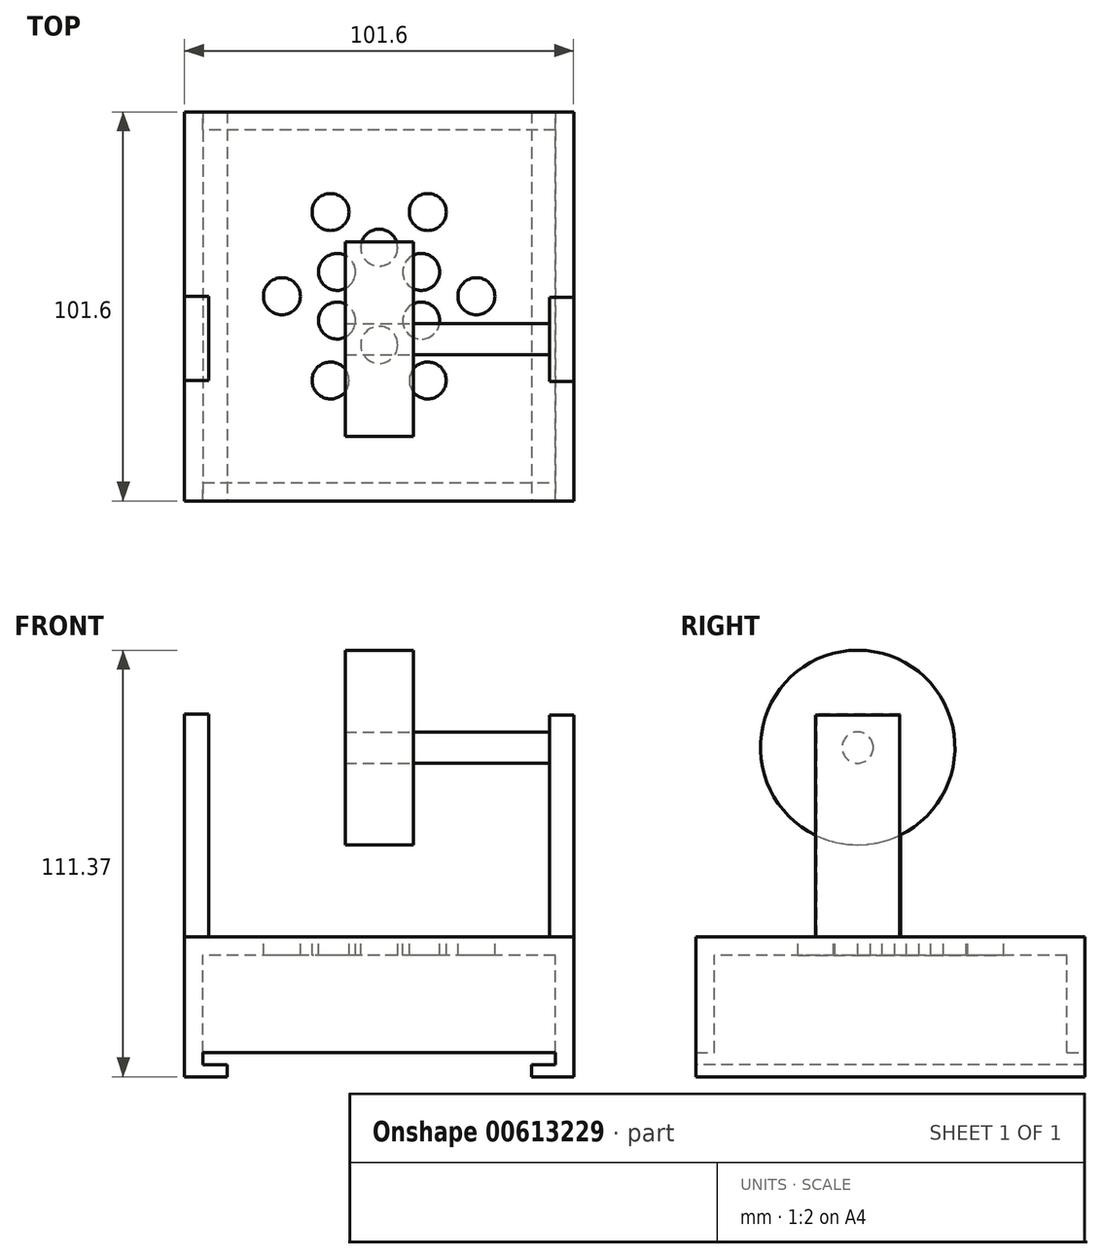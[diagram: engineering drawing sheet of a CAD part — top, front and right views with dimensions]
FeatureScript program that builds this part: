
annotation { "Feature Type Name" : "Feature", "Feature Type Description" : "" }
export const myFeature = defineFeature(function(context is Context, id is Id, definition is map)
    precondition{}
    {
        {
            var Q0;
            Q0=qCreatedBy(makeId("Top.planeOp"),FACE);
            var sketch = newSketch(context, id + "F0", { "sketchPlane" : qUnion([Q0])});
            skLineSegment(sketch, "E0", {"start": v(-108.53, 59.8) * mm, "end": v(-108.53, -41.8) * mm});
            skLineSegment(sketch, "E1", {"start": v(-108.53, -41.8) * mm, "end": v(-6.93, -41.8) * mm});
            skLineSegment(sketch, "E2", {"start": v(-6.93, -41.8) * mm, "end": v(-6.93, 59.8) * mm});
            skLineSegment(sketch, "E3", {"start": v(-6.93, 59.8) * mm, "end": v(-108.53, 59.8) * mm});
            skSolve(sketch);
        }
        {
            var Q0;
            Q0=makeQuery(id+"F0.imprint","IMPRINT",FACE,{"disambiguationData":[TD([[makeQuery(id+"F0.imprint","IMPRINT",EDGE,{"derivedFrom":sQuery(id+"F0.wireOp",EDGE,"E0")}),1.0]])]});
            extrude(context, id + "F1", {"entities" : qUnion([Q0]), "oppositeDirection" : true, "depth" : 30.16 * mm, "offsetDistance" : 25.4 * mm});
        }
        {
            var Q0;
            Q0=makeQuery(id+"F1.opExtrude","SWEPT_FACE",FACE,{"disambiguationData":[OSD([sQuery(id+"F0.wireOp",EDGE,"E2")])]});
            var sketch = newSketch(context, id + "F2", { "sketchPlane" : qUnion([Q0])});
            skLineSegment(sketch, "E4", {"start": v(-10.59, 0) * mm, "end": v(-10.59, 57.92) * mm});
            skLineSegment(sketch, "E5", {"start": v(-10.59, 57.92) * mm, "end": v(11.37, 57.92) * mm});
            skLineSegment(sketch, "E6", {"start": v(11.37, 57.92) * mm, "end": v(11.37, 0) * mm});
            skLineSegment(sketch, "E7", {"start": v(11.37, 0) * mm, "end": v(-10.59, 0) * mm});
            skSolve(sketch);
        }
        {
            var Q0;
            Q0 = qSketchRegion(id + "F2", true);
            extrude(context, id + "F3", {"entities" : qUnion([Q0]), "oppositeDirection" : true, "depth" : 6.35 * mm, "offsetDistance" : 25.4 * mm});
        }
        {
            var Q0;
            Q0=makeQuery(id+"F1.opExtrude","SWEPT_FACE",FACE,{"disambiguationData":[OSD([sQuery(id+"F0.wireOp",EDGE,"E0")])]});
            var sketch = newSketch(context, id + "F4", { "sketchPlane" : qUnion([Q0])});
            skLineSegment(sketch, "E8", {"start": v(-11.64, 0) * mm, "end": v(-11.64, 58.18) * mm});
            skLineSegment(sketch, "E9", {"start": v(-11.64, 58.18) * mm, "end": v(10.33, 58.18) * mm});
            skLineSegment(sketch, "E10", {"start": v(10.33, 58.18) * mm, "end": v(10.33, 0) * mm});
            skLineSegment(sketch, "E11", {"start": v(10.33, 0) * mm, "end": v(-11.64, 0) * mm});
            skSolve(sketch);
        }
        {
            var Q0;
            Q0=makeQuery(id+"F4.imprint","IMPRINT",FACE,{"disambiguationData":[TD([[makeQuery(id+"F4.imprint","IMPRINT",EDGE,{"derivedFrom":sQuery(id+"F4.wireOp",EDGE,"E8")}),-1.0]])]});
            extrude(context, id + "F5", {"entities" : qUnion([Q0]), "oppositeDirection" : true, "depth" : 6.35 * mm, "offsetDistance" : 25.4 * mm});
        }
        {
            var Q0;
            Q0=makeQuery(id+"F1.opExtrude","CAP_FACE",FACE,{"disambiguationData":[OSD([sQuery(id+"F0.wireOp",EDGE,"E0"),sQuery(id+"F0.wireOp",EDGE,"E1"),sQuery(id+"F0.wireOp",EDGE,"E2"),sQuery(id+"F0.wireOp",EDGE,"E3")])],"isStart":true});
            var sketch = newSketch(context, id + "F6", { "sketchPlane" : qUnion([Q0])});
            skPoint(sketch, "E12.cCircle.centerSnap0", {"position": v(-57.73, -41.8) * mm});
            skLineSegment(sketch, "E12.4", {"start": v(-70.43, 33.63) * mm, "end": v(-45.03, 33.63) * mm});
            skPoint(sketch, "E13.cCircle.perimeterSnap0", {"position": v(-57.73, -10.36) * mm});
            skPoint(sketch, "E13.0.startSnap0", {"position": v(-57.73, -10.36) * mm});
            skCircle(sketch, "E14", {"center": v(-70.43, -10.36) * mm, "radius": 4.83 * mm});
            skCircle(sketch, "E15.1.0", {"center": v(-45.03, -10.36) * mm, "radius": 4.83 * mm});
            skCircle(sketch, "E15.2.0", {"center": v(-32.33, 11.64) * mm, "radius": 4.83 * mm});
            skCircle(sketch, "E15.3.0", {"center": v(-45.03, 33.63) * mm, "radius": 4.83 * mm});
            skCircle(sketch, "E15.4.0", {"center": v(-70.43, 33.63) * mm, "radius": 4.83 * mm});
            skCircle(sketch, "E15.5.0", {"center": v(-83.13, 11.64) * mm, "radius": 4.83 * mm});
            skPoint(sketch, "E15.center", {"position": v(-57.73, 11.64) * mm});
            skCircle(sketch, "E16", {"center": v(-57.73, -1.06) * mm, "radius": 4.83 * mm});
            skCircle(sketch, "E17.1.0", {"center": v(-46.73, 5.29) * mm, "radius": 4.83 * mm});
            skCircle(sketch, "E17.2.0", {"center": v(-46.73, 17.99) * mm, "radius": 4.83 * mm});
            skCircle(sketch, "E17.3.0", {"center": v(-57.73, 24.34) * mm, "radius": 4.83 * mm});
            skCircle(sketch, "E17.4.0", {"center": v(-68.73, 17.99) * mm, "radius": 4.83 * mm});
            skCircle(sketch, "E17.5.0", {"center": v(-68.73, 5.29) * mm, "radius": 4.83 * mm});
            skSolve(sketch);
        }
        {
            var Q0;
            Q0=makeQuery(id+"F1.opExtrude","CAP_FACE",FACE,{"disambiguationData":[OSD([sQuery(id+"F0.wireOp",EDGE,"E0"),sQuery(id+"F0.wireOp",EDGE,"E1"),sQuery(id+"F0.wireOp",EDGE,"E2"),sQuery(id+"F0.wireOp",EDGE,"E3")])],"isStart":false});
            shell(context, id + "F7", {"entities" : qUnion([Q0]), "thickness" : 4.76 * mm});
        }
        {
            var Q0;
            Q0=makeQuery(id+"F6.imprint","IMPRINT",FACE,{"disambiguationData":[TD([[makeQuery(id+"F6.imprint","IMPRINT",EDGE,{"derivedFrom":sQuery(id+"F6.wireOp",EDGE,"E15.4.0")}),1.0]])]});
            var Q1;
            Q1=makeQuery(id+"F6.imprint","IMPRINT",FACE,{"disambiguationData":[TD([[makeQuery(id+"F6.imprint","IMPRINT",EDGE,{"derivedFrom":sQuery(id+"F6.wireOp",EDGE,"E15.3.0")}),1.0]])]});
            var Q2;
            Q2=makeQuery(id+"F6.imprint","IMPRINT",FACE,{"disambiguationData":[TD([[makeQuery(id+"F6.imprint","IMPRINT",EDGE,{"derivedFrom":sQuery(id+"F6.wireOp",EDGE,"E17.3.0")}),1.0]])]});
            var Q3;
            Q3=makeQuery(id+"F6.imprint","IMPRINT",FACE,{"disambiguationData":[TD([[makeQuery(id+"F6.imprint","IMPRINT",EDGE,{"derivedFrom":sQuery(id+"F6.wireOp",EDGE,"E17.2.0")}),1.0]])]});
            var Q4;
            Q4=makeQuery(id+"F6.imprint","IMPRINT",FACE,{"disambiguationData":[TD([[makeQuery(id+"F6.imprint","IMPRINT",EDGE,{"derivedFrom":sQuery(id+"F6.wireOp",EDGE,"E17.1.0")}),1.0]])]});
            var Q5;
            Q5=makeQuery(id+"F6.imprint","IMPRINT",FACE,{"disambiguationData":[TD([[makeQuery(id+"F6.imprint","IMPRINT",EDGE,{"derivedFrom":sQuery(id+"F6.wireOp",EDGE,"E15.2.0")}),1.0]])]});
            var Q6;
            Q6=makeQuery(id+"F6.imprint","IMPRINT",FACE,{"disambiguationData":[TD([[makeQuery(id+"F6.imprint","IMPRINT",EDGE,{"derivedFrom":sQuery(id+"F6.wireOp",EDGE,"E15.1.0")}),1.0]])]});
            var Q7;
            Q7=makeQuery(id+"F6.imprint","IMPRINT",FACE,{"disambiguationData":[TD([[makeQuery(id+"F6.imprint","IMPRINT",EDGE,{"derivedFrom":sQuery(id+"F6.wireOp",EDGE,"E16")}),1.0]])]});
            var Q8;
            Q8=makeQuery(id+"F6.imprint","IMPRINT",FACE,{"disambiguationData":[TD([[makeQuery(id+"F6.imprint","IMPRINT",EDGE,{"derivedFrom":sQuery(id+"F6.wireOp",EDGE,"E14")}),1.0]])]});
            var Q9;
            Q9=makeQuery(id+"F6.imprint","IMPRINT",FACE,{"disambiguationData":[TD([[makeQuery(id+"F6.imprint","IMPRINT",EDGE,{"derivedFrom":sQuery(id+"F6.wireOp",EDGE,"E17.5.0")}),1.0]])]});
            var Q10;
            Q10=makeQuery(id+"F6.imprint","IMPRINT",FACE,{"disambiguationData":[TD([[makeQuery(id+"F6.imprint","IMPRINT",EDGE,{"derivedFrom":sQuery(id+"F6.wireOp",EDGE,"E17.4.0")}),1.0]])]});
            var Q11;
            Q11=makeQuery(id+"F6.imprint","IMPRINT",FACE,{"disambiguationData":[TD([[makeQuery(id+"F6.imprint","IMPRINT",EDGE,{"derivedFrom":sQuery(id+"F6.wireOp",EDGE,"E15.5.0")}),1.0]])]});
            extrude(context, id + "F8", {"entities" : qUnion([Q0, Q1, Q2, Q3, Q4, Q5, Q6, Q7, Q8, Q9, Q10, Q11]), "operationType" : NewBodyOperationType.REMOVE, "oppositeDirection" : true, "depth" : 65.53 * mm, "offsetDistance" : 25.4 * mm});
        }
        {
            var Q0;
            Q0=makeQuery(id+"F1.opExtrude","CAP_FACE",FACE,{"disambiguationData":[OSD([sQuery(id+"F0.wireOp",EDGE,"E0"),sQuery(id+"F0.wireOp",EDGE,"E1"),sQuery(id+"F0.wireOp",EDGE,"E2"),sQuery(id+"F0.wireOp",EDGE,"E3")])],"isStart":false});
            var sketch = newSketch(context, id + "F9", { "sketchPlane" : qUnion([Q0])});
            skLineSegment(sketch, "E18", {"start": v(-108.53, 41.8) * mm, "end": v(-103.76, 41.8) * mm});
            skLineSegment(sketch, "E19", {"start": v(-103.76, 41.8) * mm, "end": v(-103.76, -59.8) * mm});
            skLineSegment(sketch, "E20", {"start": v(-103.76, -59.8) * mm, "end": v(-108.53, -59.8) * mm});
            skLineSegment(sketch, "E21", {"start": v(-108.53, -59.8) * mm, "end": v(-108.53, 41.8) * mm});
            skLineSegment(sketch, "E22", {"start": v(-6.93, 41.8) * mm, "end": v(-11.69, 41.8) * mm});
            skLineSegment(sketch, "E23", {"start": v(-11.69, 41.8) * mm, "end": v(-11.69, -59.8) * mm});
            skLineSegment(sketch, "E24", {"start": v(-11.69, -59.8) * mm, "end": v(-6.93, -59.8) * mm});
            skLineSegment(sketch, "E25", {"start": v(-6.93, -59.8) * mm, "end": v(-6.93, 41.8) * mm});
            skSolve(sketch);
        }
        {
            var Q0;
            Q0 = qSketchRegion(id + "F9", true);
            extrude(context, id + "F10", {"entities" : qUnion([Q0]), "operationType" : NewBodyOperationType.ADD, "depth" : 6.35 * mm, "offsetDistance" : 25.4 * mm});
        }
        {
            var Q0;
            Q0=makeQuery(id+"F10.boolean.opBoolean","MERGE",FACE,{"derivedFrom":[makeQuery(id+"F1.opExtrude","SWEPT_FACE",FACE,{"disambiguationData":[OSD([sQuery(id+"F0.wireOp",EDGE,"E1")])]}),makeQuery(id+"F10.opExtrude","SWEPT_FACE",FACE,{"disambiguationData":[OSD([sQuery(id+"F9.wireOp",EDGE,"E18")])]}),makeQuery(id+"F10.opExtrude","SWEPT_FACE",FACE,{"disambiguationData":[OSD([sQuery(id+"F9.wireOp",EDGE,"E22")])]})]});
            var sketch = newSketch(context, id + "F11", { "sketchPlane" : qUnion([Q0])});
            skLineSegment(sketch, "E26", {"start": v(-11.69, -36.51) * mm, "end": v(-17.9, -36.51) * mm});
            skLineSegment(sketch, "E27", {"start": v(-17.9, -36.51) * mm, "end": v(-17.9, -33.34) * mm});
            skLineSegment(sketch, "E28", {"start": v(-17.9, -33.34) * mm, "end": v(-11.69, -33.34) * mm});
            skLineSegment(sketch, "E29", {"start": v(-103.76, -36.51) * mm, "end": v(-103.76, -33.34) * mm});
            skLineSegment(sketch, "E30", {"start": v(-103.76, -33.34) * mm, "end": v(-97.38, -33.34) * mm});
            skLineSegment(sketch, "E31", {"start": v(-97.38, -33.34) * mm, "end": v(-97.38, -36.51) * mm});
            skLineSegment(sketch, "E32", {"start": v(-97.38, -36.51) * mm, "end": v(-103.76, -36.51) * mm});
            skSolve(sketch);
        }
        {
            var Q0;
            Q0 = qSketchRegion(id + "F11", true);
            var Q1;
            {var subQ0=sQuery(id+"F11.wireOp",EDGE,"E26");Q1=makeQuery(id+"F11.imprint","IMPRINT",FACE,{"disambiguationData":[TD([[makeQuery(id+"F11.imprint","IMPRINT",EDGE,{"derivedFrom":subQ0}),-1.0]])]});}
            extrude(context, id + "F12", {"entities" : qUnion([Q0, Q1]), "operationType" : NewBodyOperationType.ADD, "oppositeDirection" : true, "depth" : 101.6 * mm, "offsetDistance" : 25.4 * mm});
        }
        {
            var Q0;
            Q0=makeQuery(id+"F5.opExtrude","CAP_FACE",FACE,{"disambiguationData":[OSD([sQuery(id+"F4.wireOp",EDGE,"E8"),sQuery(id+"F4.wireOp",EDGE,"E9"),sQuery(id+"F4.wireOp",EDGE,"E10"),sQuery(id+"F4.wireOp",EDGE,"E11")])],"isStart":false});
            var sketch = newSketch(context, id + "F13", { "sketchPlane" : qUnion([Q0])});
            skCircle(sketch, "E33", {"center": v(0.65, 48.95) * mm, "radius": 4.14 * mm});
            skPoint(sketch, "E33.centerSnap0", {"position": v(0.65, 58.18) * mm});
            skSolve(sketch);
        }
        {
            var Q0;
            Q0=sQuery(id+"F13.wireOp",EDGE,"E33");
            extrude(context, id + "F14", {"bodyType" : ToolBodyType.SURFACE, "surfaceEntities" : qUnion([Q0]), "endBound" : BoundingType.UP_TO_NEXT, "depth" : 35.56 * mm, "offsetDistance" : 25.4 * mm});
        }
        {
            var Q0;
            Q0=makeQuery(id+"F3.opExtrude","CAP_FACE",FACE,{"disambiguationData":[OSD([sQuery(id+"F2.wireOp",EDGE,"E4"),sQuery(id+"F2.wireOp",EDGE,"E5"),sQuery(id+"F2.wireOp",EDGE,"E6"),sQuery(id+"F2.wireOp",EDGE,"E7")])],"isStart":false});
            var sketch = newSketch(context, id + "F15", { "sketchPlane" : qUnion([Q0])});
            skCircle(sketch, "E34", {"center": v(-0.4, 49.46) * mm, "radius": 4.06 * mm});
            skPoint(sketch, "E34.centerSnap0", {"position": v(-0.4, 57.92) * mm});
            skSolve(sketch);
        }
        {
            var Q0;
            Q0=makeQuery(id+"F15.imprint","IMPRINT",FACE,{"disambiguationData":[TD([[makeQuery(id+"F15.imprint","IMPRINT",EDGE,{"derivedFrom":sQuery(id+"F15.wireOp",EDGE,"E34")}),1.0]])]});
            extrude(context, id + "F16", {"entities" : qUnion([Q0]), "operationType" : NewBodyOperationType.ADD, "depth" : 35.56 * mm, "offsetDistance" : 25.4 * mm});
        }
        {
            var Q0;
            Q0=makeQuery(id+"F16.opExtrude","CAP_FACE",FACE,{"disambiguationData":[OSD([sQuery(id+"F15.wireOp",EDGE,"E34")])],"isStart":false});
            var sketch = newSketch(context, id + "F17", { "sketchPlane" : qUnion([Q0])});
            skCircle(sketch, "E35", {"center": v(-0.4, 49.46) * mm, "radius": 25.4 * mm});
            skSolve(sketch);
        }
        {
            var Q0;
            Q0=makeQuery(id+"F17.imprint","IMPRINT",FACE,{"disambiguationData":[TD([[makeQuery(id+"F17.imprint","IMPRINT",EDGE,{"derivedFrom":sQuery(id+"F17.wireOp",EDGE,"E35")}),1.0]])]});
            extrude(context, id + "F18", {"entities" : qUnion([Q0]), "depth" : 17.78 * mm, "offsetDistance" : 25.4 * mm});
        }
    });
